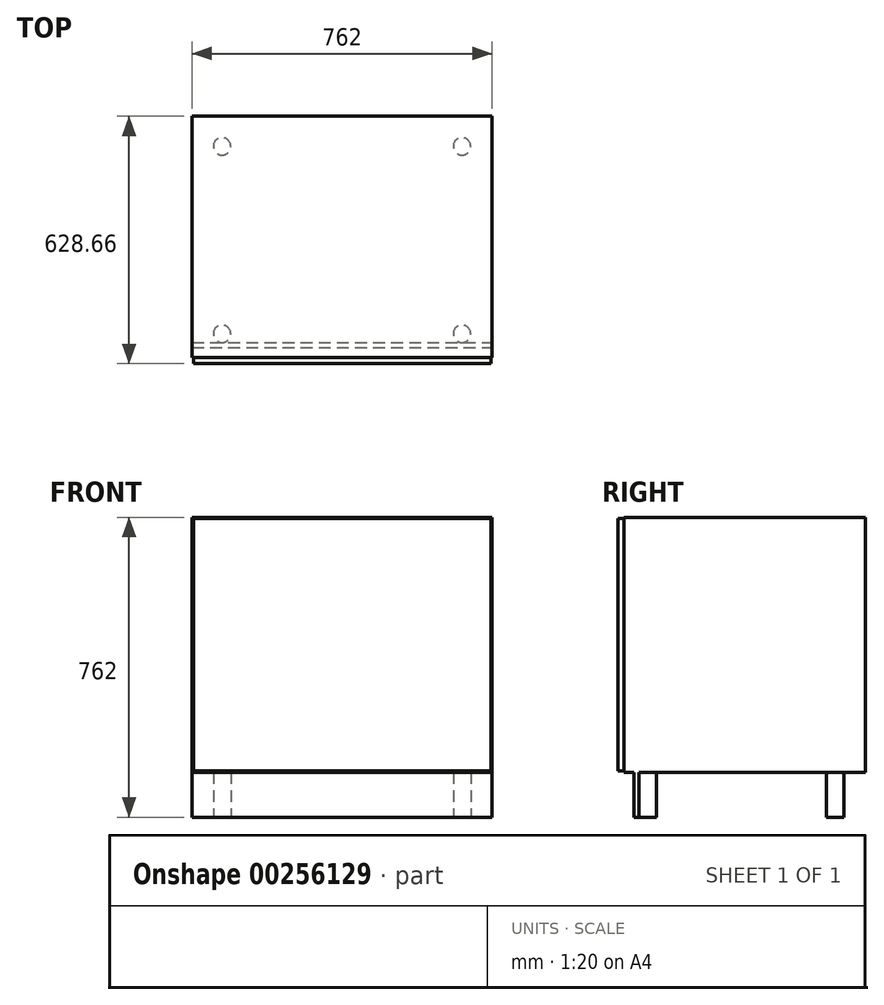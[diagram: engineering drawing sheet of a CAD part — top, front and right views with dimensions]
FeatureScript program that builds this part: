
annotation { "Feature Type Name" : "Feature", "Feature Type Description" : "" }
export const myFeature = defineFeature(function(context is Context, id is Id, definition is map)
    precondition{}
    {
        {
            var Q0;
            Q0=qCreatedBy(makeId("Front.planeOp"),FACE);
            var sketch = newSketch(context, id + "F0", { "sketchPlane" : qUnion([Q0])});
            skLineSegment(sketch, "E0.bottom", {"start": v(381, 114.3) * mm, "end": v(-381, 114.3) * mm});
            skLineSegment(sketch, "E0.top", {"start": v(381, 762) * mm, "end": v(-381, 762) * mm});
            skLineSegment(sketch, "E0.left", {"start": v(381, 114.3) * mm, "end": v(381, 762) * mm});
            skLineSegment(sketch, "E0.right", {"start": v(-381, 114.3) * mm, "end": v(-381, 762) * mm});
            skPoint(sketch, "E0.middle", {"position": v(0, 438.15) * mm});
            skSolve(sketch);
        }
        {
            var Q0;
            Q0 = qSketchRegion(id + "F0", true);
            extrude(context, id + "F1", {"entities" : qUnion([Q0]), "endBound" : BoundingType.SYMMETRIC, "oppositeDirection" : true, "depth" : 628.65 * mm});
        }
        {
            var Q0;
            Q0=qCreatedBy(makeId("Top.planeOp"),FACE);
            var sketch = newSketch(context, id + "F2", { "sketchPlane" : qUnion([Q0])});
            skCircle(sketch, "E1", {"center": v(-304.8, -238.13) * mm, "radius": 22.23 * mm});
            skCircle(sketch, "E2.MirrorC", {"center": v(304.8, -238.13) * mm, "radius": 22.23 * mm});
            skCircle(sketch, "E3.MirrorC", {"center": v(304.8, 238.13) * mm, "radius": 22.23 * mm});
            skCircle(sketch, "E4.MirrorC", {"center": v(-304.8, 238.13) * mm, "radius": 22.23 * mm});
            skSolve(sketch);
        }
        {
            var Q0;
            Q0 = qSketchRegion(id + "F2", true);
            extrude(context, id + "F3", {"entities" : qUnion([Q0]), "operationType" : NewBodyOperationType.ADD, "depth" : 114.3 * mm});
        }
        {
            var Q0;
            Q0=qCreatedBy(makeId("Top.planeOp"),FACE);
            var sketch = newSketch(context, id + "F4", { "sketchPlane" : qUnion([Q0])});
            skLineSegment(sketch, "E5.bottom", {"start": v(-381, -260.6) * mm, "end": v(381, -260.6) * mm});
            skLineSegment(sketch, "E5.top", {"start": v(-381, -273.3) * mm, "end": v(381, -273.3) * mm});
            skLineSegment(sketch, "E5.left", {"start": v(-381, -260.6) * mm, "end": v(-381, -273.3) * mm});
            skLineSegment(sketch, "E5.right", {"start": v(381, -260.6) * mm, "end": v(381, -273.3) * mm});
            skPoint(sketch, "E5.middle", {"position": v(0, -266.95) * mm});
            skSolve(sketch);
        }
        {
            var Q0;
            Q0 = qSketchRegion(id + "F4", true);
            extrude(context, id + "F5", {"entities" : qUnion([Q0]), "operationType" : NewBodyOperationType.ADD, "endBound" : BoundingType.UP_TO_NEXT, "depth" : 25.4 * mm});
        }
        {
            var Q0;
            Q0=makeQuery(id+"F1.opExtrude","CAP_FACE",FACE,{"disambiguationData":[OSD([sQuery(id+"F0.wireOp",EDGE,"E0.bottom"),sQuery(id+"F0.wireOp",EDGE,"E0.top"),sQuery(id+"F0.wireOp",EDGE,"E0.left"),sQuery(id+"F0.wireOp",EDGE,"E0.right")])],"isStart":true});
            var sketch = newSketch(context, id + "F6", { "sketchPlane" : qUnion([Q0])});
            skLineSegment(sketch, "E6.0", {"start": v(377.83, 117.48) * mm, "end": v(377.82, 758.83) * mm});
            skLineSegment(sketch, "E6.1", {"start": v(-377.82, 117.47) * mm, "end": v(377.83, 117.48) * mm});
            skLineSegment(sketch, "E6.2", {"start": v(-377.83, 758.83) * mm, "end": v(-377.83, 117.47) * mm});
            skLineSegment(sketch, "E6.3", {"start": v(377.82, 758.83) * mm, "end": v(-377.83, 758.83) * mm});
            skSolve(sketch);
        }
        {
            var Q0;
            Q0=makeQuery(id+"F6.imprint","IMPRINT",FACE,{"disambiguationData":[TD([[makeQuery(id+"F6.imprint","IMPRINT",EDGE,{"derivedFrom":sQuery(id+"F6.wireOp",EDGE,"E6.0")}),-1.0]])]});
            extrude(context, id + "F7", {"entities" : qUnion([Q0]), "operationType" : NewBodyOperationType.REMOVE, "oppositeDirection" : true, "depth" : 15.88 * mm});
        }
    });
